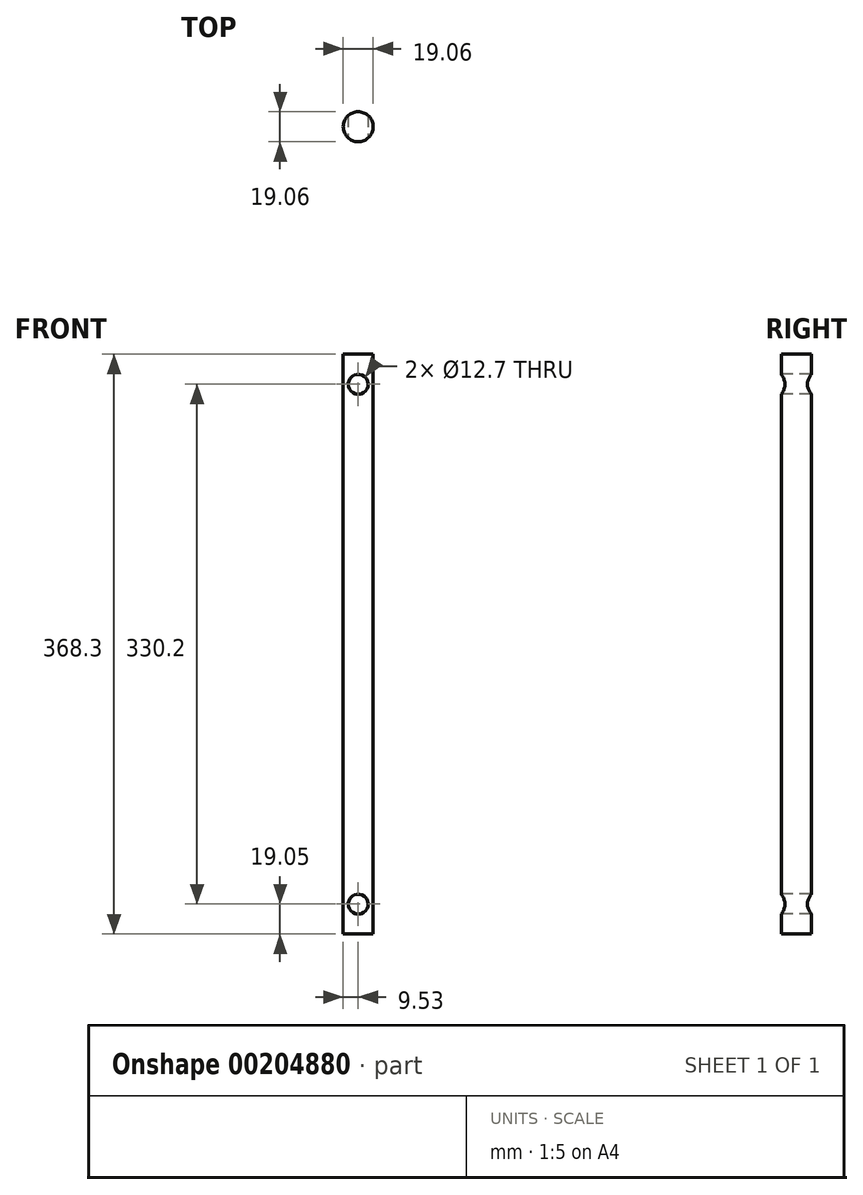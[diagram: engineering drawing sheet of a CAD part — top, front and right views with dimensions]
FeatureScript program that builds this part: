
annotation { "Feature Type Name" : "Feature", "Feature Type Description" : "" }
export const myFeature = defineFeature(function(context is Context, id is Id, definition is map)
    precondition{}
    {
        {
            var Q0;
            Q0=qCreatedBy(makeId("Top.planeOp"),FACE);
            var sketch = newSketch(context, id + "F0", { "sketchPlane" : qUnion([Q0])});
            skCircle(sketch, "E0", {"center": v(0, 0) * mm, "radius": 9.53 * mm});
            skSolve(sketch);
        }
        {
            var Q0;
            Q0 = qSketchRegion(id + "F0", true);
            extrude(context, id + "F1", {"entities" : qUnion([Q0]), "endBound" : BoundingType.SYMMETRIC, "depth" : 368.3 * mm});
        }
        {
            var Q0;
            Q0=qCreatedBy(makeId("Front.planeOp"),FACE);
            var sketch = newSketch(context, id + "F2", { "sketchPlane" : qUnion([Q0])});
            skCircle(sketch, "E1", {"center": v(0, -165.1) * mm, "radius": 6.35 * mm});
            skCircle(sketch, "E2", {"center": v(0, 165.1) * mm, "radius": 6.35 * mm});
            skSolve(sketch);
        }
        {
            var Q0;
            Q0 = qSketchRegion(id + "F2", true);
            extrude(context, id + "F3", {"entities" : qUnion([Q0]), "operationType" : NewBodyOperationType.REMOVE, "endBound" : BoundingType.SYMMETRIC, "oppositeDirection" : true, "depth" : 25.4 * mm});
        }
    });
